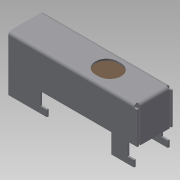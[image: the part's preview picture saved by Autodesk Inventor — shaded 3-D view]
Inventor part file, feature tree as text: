
AUTODESK INVENTOR PART (.ipt)
format: ipt  version: 2016 (Build 200138000, 138)  size: 200,192 bytes
history: native  units: mm
features: sheet_metal_op x7, sketch x5, reference x5, other x3, extrude x2, fillet x2, plane x1, chamfer x1
ambient origin geometry x8: Origin, YZ Plane, XZ Plane, XY Plane, X Axis, Y Axis, Z Axis, Center Point
bodies: Solid1 (feature_tree)
feature tree (26):
  plane  "Work Plane1"
  sheet_metal_op  "Face1"
  sheet_metal_op  "Flange1"
  sketch  "Sketch3"  dims[d4=1.0mm]
  sheet_metal_op  "Flange2"
  extrude  "Extrusion1"  Depth=0.5mm
  extrude  "Extrusion5"  Depth=0.5mm
  chamfer  "Chamfer1"  Distance=17.0mm Angle=90.0deg
  fillet  "Fillet1"  Radius=2.0mm
  fillet  "Fillet2"  Radius=0.5mm
  sketch  "Sketch1"  dims[d0=7.0mm d1=0.5mm]
  reference  "Reference1"
  reference  "Reference2"
  reference  "Reference3"
  reference  "Reference4"
  reference  "Reference5"
  other  "Plate1"
  sketch  "Sketch2"  dims[d2=0.5mm d3=0.25mm]
  other  "Plate2"
  sheet_metal_op  "Bend1"
  sheet_metal_op  "Corner1"
  sketch  "Sketch4"  dims[d5=0.5mm d6=17.0mm d7=90.0deg d8=0.5mm d9=2.0mm d10=0.5mm]
  other  "Plate3"
  sheet_metal_op  "Bend2"
  sheet_metal_op  "Corner2"
  sketch  "Sketch8"  dims[d11=0.5mm d13=20.0mm d14=0.5mm d15=0.25mm d16=1.0mm d17=0.5mm d18=11.0mm d19=90.0deg d20=0.5mm d21=2.0mm d22=0.5mm d23=0.5mm d24=15.0mm d25=0.0mm d28=3.0mm d32=40.0mm d37=6.0mm d38=4.0mm d39=3.0mm d40=5.0mm d41=2.0mm d42=2.0mm d43=1.0mm d44=7.0mm d45=1.0mm d46=14.0mm d47=0.0mm d48=1.5mm d49=2.0mm d50=45.0deg d51=0.5mm d52=0.5mm]
